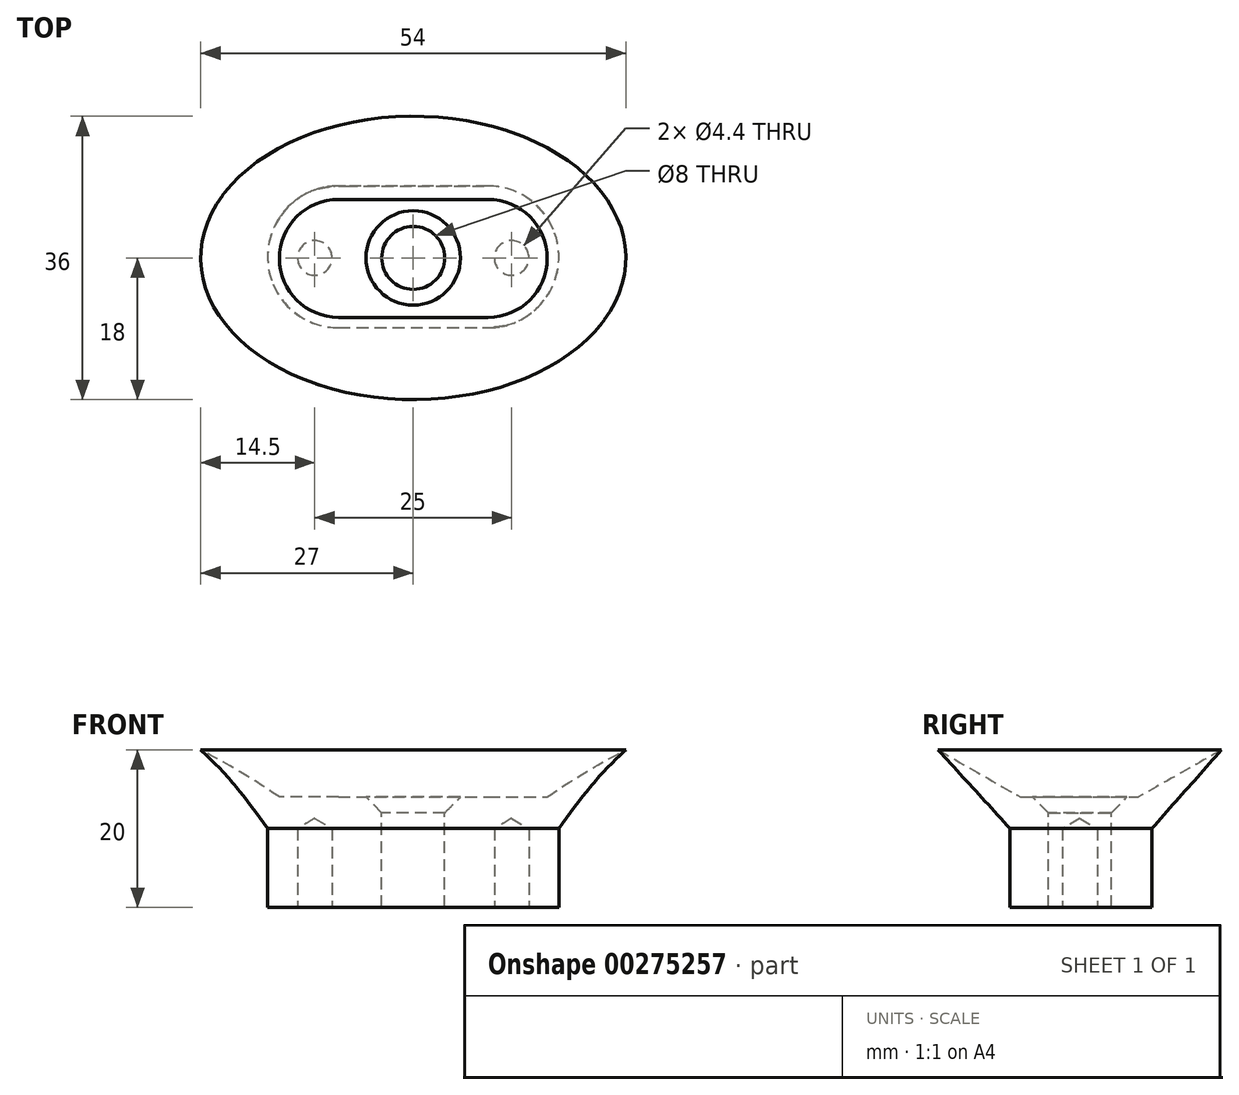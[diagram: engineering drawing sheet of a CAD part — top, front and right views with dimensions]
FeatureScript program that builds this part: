
annotation { "Feature Type Name" : "Feature", "Feature Type Description" : "" }
export const myFeature = defineFeature(function(context is Context, id is Id, definition is map)
    precondition{}
    {
        {
            var Q0;
            Q0=qCreatedBy(makeId("Top.planeOp"),FACE);
            var sketch = newSketch(context, id + "F0", { "sketchPlane" : qUnion([Q0])});
            skEllipse(sketch, "E0", {"center": v(0, 0) * mm, "majorRadius": 27 * mm, "minorRadius": 18 * mm, "majorAxis": v(1, 0)});
            skSolve(sketch);
        }
        {
            var Q0;
            Q0=makeQuery(id+"F0.imprint","IMPRINT",FACE,{"disambiguationData":[TD([[makeQuery(id+"F0.imprint","IMPRINT",EDGE,{"derivedFrom":sQuery(id+"F0.wireOp",EDGE,"E0")}),1.0]])]});
            cPlane(context, id + "F1", {"entities" : qUnion([Q0]), "cplaneType" : CPlaneType.OFFSET, "offset" : 10 * mm, "oppositeDirection" : true, "width" : 150 * mm, "height" : 150 * mm});
        }
        {
            var Q0;
            Q0=qCreatedBy(id+"F1.planeOp",FACE);
            var sketch = newSketch(context, id + "F2", { "sketchPlane" : qUnion([Q0])});
            skLineSegment(sketch, "E1", {"start": v(-39.6, 0) * mm, "end": v(40.18, 0) * mm, "construction": true});
            skLineSegment(sketch, "E2", {"start": v(0, -11.83) * mm, "end": v(0, 12.05) * mm, "construction": true});
            skLineSegment(sketch, "E3.0", {"start": v(-9.5, -8.87) * mm, "end": v(9.5, -8.87) * mm});
            skArc(sketch, "E3.1", {"start": v(-9.5, 9.13) * mm, "mid": v(-18.5, 0.13) * mm, "end": v(-9.5, -8.87) * mm});
            skLineSegment(sketch, "E3.2", {"start": v(-9.5, 9.13) * mm, "end": v(9.5, 9.13) * mm});
            skArc(sketch, "E3.3", {"start": v(9.5, -8.87) * mm, "mid": v(18.5, 0.13) * mm, "end": v(9.5, 9.13) * mm});
            skSolve(sketch);
        }
        {
            var Q0;
            Q0=makeQuery(id+"F0.imprint","IMPRINT",FACE,{"disambiguationData":[TD([[makeQuery(id+"F0.imprint","IMPRINT",EDGE,{"derivedFrom":sQuery(id+"F0.wireOp",EDGE,"E0")}),1.0]])]});
            var Q1;
            Q1=makeQuery(id+"F2.imprint","IMPRINT",FACE,{"disambiguationData":[TD([[makeQuery(id+"F2.imprint","IMPRINT",EDGE,{"derivedFrom":sQuery(id+"F2.wireOp",EDGE,"E3.0")}),1.0]])]});
            loft(context, id + "F3", {"sheetProfilesArray" : [{ "sheetProfileEntities" : qUnion([Q0]) }, { "sheetProfileEntities" : qUnion([Q1]) }]});
        }
        {
            var Q0;
            Q0=makeQuery(id+"F0.imprint","IMPRINT",FACE,{"disambiguationData":[TD([[makeQuery(id+"F0.imprint","IMPRINT",EDGE,{"derivedFrom":sQuery(id+"F0.wireOp",EDGE,"E0")}),1.0]])]});
            cPlane(context, id + "F4", {"entities" : qUnion([Q0]), "cplaneType" : CPlaneType.OFFSET, "offset" : 6 * mm, "oppositeDirection" : true, "width" : 150 * mm, "height" : 150 * mm});
        }
        {
            var Q0;
            Q0=qCreatedBy(id+"F4.planeOp",FACE);
            var sketch = newSketch(context, id + "F5", { "sketchPlane" : qUnion([Q0])});
            skLineSegment(sketch, "E4", {"start": v(-26.9, 0) * mm, "end": v(26.14, 0) * mm, "construction": true});
            skLineSegment(sketch, "E5", {"start": v(-9.5, -7.56) * mm, "end": v(9.5, -7.56) * mm});
            skLineSegment(sketch, "E6", {"start": v(-9.5, 7.44) * mm, "end": v(9.5, 7.44) * mm});
            skArc(sketch, "E7", {"start": v(-9.5, 7.44) * mm, "mid": v(-17, -0.06) * mm, "end": v(-9.5, -7.56) * mm});
            skArc(sketch, "E8", {"start": v(9.5, -7.56) * mm, "mid": v(17, -0.06) * mm, "end": v(9.5, 7.44) * mm});
            skSolve(sketch);
        }
        {
            var Q1;
            Q1 = qSketchRegion(id + "F0", true);
            var Q2;
            Q2 = qSketchRegion(id + "F5", true);
            loft(context, id + "F6", {"operationType" : NewBodyOperationType.REMOVE, "sheetProfilesArray" : [{ "sheetProfileEntities" : qUnion([Q1]) }, { "sheetProfileEntities" : qUnion([Q2]) }]});
        }
        {
            var Q0;
            Q0=makeQuery(id+"F3.opLoft","CAP_FACE",FACE,{"disambiguationData":[OSD([makeQuery(id+"F2.imprint","IMPRINT",FACE,{"disambiguationData":[TD([[makeQuery(id+"F2.imprint","IMPRINT",EDGE,{"derivedFrom":sQuery(id+"F2.wireOp",EDGE,"E3.0")}),1.0]])]})])],"isStart":true});
            var sketch = newSketch(context, id + "F7", { "sketchPlane" : qUnion([Q0])});
            skLineSegment(sketch, "E9.0.0", {"start": v(9.5, 8.87) * mm, "end": v(-9.5, 8.87) * mm});
            skFitSpline(sketch, "E9.0.1", {"points": [v(-9.5, 8.87) * mm, v(-10.1, 8.87) * mm, v(-10.68, 8.81) * mm, v(-11.26, 8.7) * mm, v(-11.84, 8.58) * mm, v(-12.4, 8.4) * mm, v(-12.94, 8.18) * mm, v(-13.49, 7.96) * mm, v(-14, 7.68) * mm, v(-14.5, 7.35) * mm, v(-15, 7.02) * mm, v(-15.45, 6.65) * mm, v(-15.86, 6.23) * mm, v(-16.28, 5.81) * mm, v(-16.65, 5.36) * mm, v(-16.98, 4.87) * mm, v(-17.31, 4.38) * mm, v(-17.59, 3.86) * mm, v(-17.81, 3.31) * mm, v(-18.04, 2.77) * mm, v(-18.21, 2.2) * mm, v(-18.33, 1.62) * mm, v(-18.44, 1.04) * mm, v(-18.5, 0.46) * mm, v(-18.5, -0.13) * mm, v(-18.5, -0.72) * mm, v(-18.44, -1.3) * mm, v(-18.33, -1.89) * mm, v(-18.21, -2.47) * mm, v(-18.04, -3.03) * mm, v(-17.81, -3.58) * mm, v(-17.59, -4.12) * mm, v(-17.31, -4.64) * mm, v(-16.98, -5.13) * mm, v(-16.66, -5.62) * mm, v(-16.28, -6.08) * mm, v(-15.86, -6.5) * mm, v(-15.45, -6.91) * mm, v(-15, -7.29) * mm, v(-14.5, -7.62) * mm, v(-14, -7.94) * mm, v(-13.5, -8.22) * mm, v(-12.94, -8.45) * mm, v(-12.4, -8.67) * mm, v(-11.84, -8.84) * mm, v(-11.26, -8.96) * mm, v(-10.68, -9.07) * mm, v(-10.1, -9.13) * mm, v(-9.5, -9.13) * mm]});
            skLineSegment(sketch, "E9.0.2", {"start": v(-9.5, -9.13) * mm, "end": v(9.5, -9.13) * mm});
            skFitSpline(sketch, "E9.0.3", {"points": [v(9.5, -9.13) * mm, v(10.1, -9.13) * mm, v(10.68, -9.07) * mm, v(11.26, -8.96) * mm, v(11.84, -8.84) * mm, v(12.4, -8.67) * mm, v(12.94, -8.45) * mm, v(13.49, -8.22) * mm, v(14, -7.94) * mm, v(14.5, -7.62) * mm, v(15, -7.29) * mm, v(15.45, -6.91) * mm, v(15.86, -6.5) * mm, v(16.28, -6.08) * mm, v(16.65, -5.62) * mm, v(16.98, -5.13) * mm, v(17.31, -4.64) * mm, v(17.59, -4.12) * mm, v(17.81, -3.58) * mm, v(18.04, -3.03) * mm, v(18.21, -2.47) * mm, v(18.33, -1.89) * mm, v(18.44, -1.3) * mm, v(18.5, -0.72) * mm, v(18.5, -0.13) * mm, v(18.5, 0.46) * mm, v(18.44, 1.04) * mm, v(18.33, 1.62) * mm, v(18.21, 2.2) * mm, v(18.04, 2.77) * mm, v(17.81, 3.31) * mm, v(17.59, 3.86) * mm, v(17.31, 4.38) * mm, v(16.98, 4.87) * mm, v(16.66, 5.36) * mm, v(16.28, 5.81) * mm, v(15.86, 6.23) * mm, v(15.45, 6.65) * mm, v(15, 7.02) * mm, v(14.5, 7.35) * mm, v(14, 7.68) * mm, v(13.5, 7.96) * mm, v(12.94, 8.18) * mm, v(12.4, 8.4) * mm, v(11.84, 8.58) * mm, v(11.26, 8.7) * mm, v(10.68, 8.81) * mm, v(10.1, 8.87) * mm, v(9.5, 8.87) * mm]});
            skSolve(sketch);
        }
        {
            var Q0;
            Q0=makeQuery(id+"F7.imprint","IMPRINT",FACE,{"disambiguationData":[TD([[makeQuery(id+"F7.imprint","IMPRINT",EDGE,{"derivedFrom":sQuery(id+"F7.wireOp",EDGE,"E9.0.0")}),1.0]])]});
            extrude(context, id + "F8", {"entities" : qUnion([Q0]), "operationType" : NewBodyOperationType.ADD, "depth" : 10 * mm});
        }
        {
            var Q0;
            Q0=qCreatedBy(id+"F4.planeOp",FACE);
            var sketch = newSketch(context, id + "F9", { "sketchPlane" : qUnion([Q0])});
            skPoint(sketch, "E10.0", {"position": v(0, 0) * mm});
            skSolve(sketch);
        }
        {
            var Q0;
            Q0=sQuery(id+"F9.wireOp",VERTEX,"E10.0");
            var Q1;
            Q1=makeQuery(id+"F3.opLoft","SWEPT_BODY",BODY,{"disambiguationData":[OSD([makeQuery(id+"F0.imprint","IMPRINT",FACE,{"disambiguationData":[TD([[makeQuery(id+"F0.imprint","IMPRINT",EDGE,{"derivedFrom":sQuery(id+"F0.wireOp",EDGE,"E0")}),1.0]])]}),makeQuery(id+"F2.imprint","IMPRINT",FACE,{"disambiguationData":[TD([[makeQuery(id+"F2.imprint","IMPRINT",EDGE,{"derivedFrom":sQuery(id+"F2.wireOp",EDGE,"E3.0")}),1.0]])]})])]});
            hole(context, id + "F10", {"style" : HoleStyle.C_SINK, "endStyle" : HoleEndStyle.THROUGH, "holeDiameter" : 8 * mm, "cSinkDiameter" : 12 * mm, "cSinkAngle" : 90 * degree, "tappedDepth" : 19.25 * mm, "tapClearance" : 3, "startFromSketch" : true, "locations" : qUnion([Q0]), "scope" : qUnion([Q1])});
        }
        {
            var Q0;
            Q0=makeQuery(id+"F8.opExtrude","CAP_FACE",FACE,{"disambiguationData":[OSD([sQuery(id+"F7.wireOp",EDGE,"E9.0.0"),sQuery(id+"F7.wireOp",EDGE,"E9.0.1"),sQuery(id+"F7.wireOp",EDGE,"E9.0.2"),sQuery(id+"F7.wireOp",EDGE,"E9.0.3")])],"isStart":false});
            var sketch = newSketch(context, id + "F11", { "sketchPlane" : qUnion([Q0])});
            skLineSegment(sketch, "E11", {"start": v(17.77, 0) * mm, "end": v(-20.35, 0) * mm, "construction": true});
            skPoint(sketch, "E12", {"position": v(12.5, 0) * mm});
            skPoint(sketch, "E13", {"position": v(-12.5, 0) * mm});
            skSolve(sketch);
        }
        {
            var Q0;
            Q0=sQuery(id+"F11.wireOp",VERTEX,"E12");
            var Q1;
            Q1=sQuery(id+"F11.wireOp",VERTEX,"E13");
            var Q2;
            Q2=makeQuery(id+"F3.opLoft","SWEPT_BODY",BODY,{"disambiguationData":[OSD([makeQuery(id+"F0.imprint","IMPRINT",FACE,{"disambiguationData":[TD([[makeQuery(id+"F0.imprint","IMPRINT",EDGE,{"derivedFrom":sQuery(id+"F0.wireOp",EDGE,"E0")}),1.0]])]}),makeQuery(id+"F2.imprint","IMPRINT",FACE,{"disambiguationData":[TD([[makeQuery(id+"F2.imprint","IMPRINT",EDGE,{"derivedFrom":sQuery(id+"F2.wireOp",EDGE,"E3.0")}),1.0]])]})])]});
            hole(context, id + "F12", {"style" : HoleStyle.SIMPLE, "endStyle" : HoleEndStyle.BLIND, "standardTappedOrClearance" : lookupTablePath({ "standard" : "ISO", "fit" : "Normal", "size" : "M4", "type" : "Clearance" }), "standardBlindInLast" : lookupTablePath({ "fit" : "Standard", "standard" : "ISO", "size" : "M4", "type" : "Clearance" }), "holeDiameter" : 4.4 * mm, "holeDepth" : 10 * mm, "tappedDepth" : 19.25 * mm, "tapClearance" : 3, "startFromSketch" : true, "locations" : qUnion([Q0, Q1]), "scope" : qUnion([Q2])});
        }
    });
